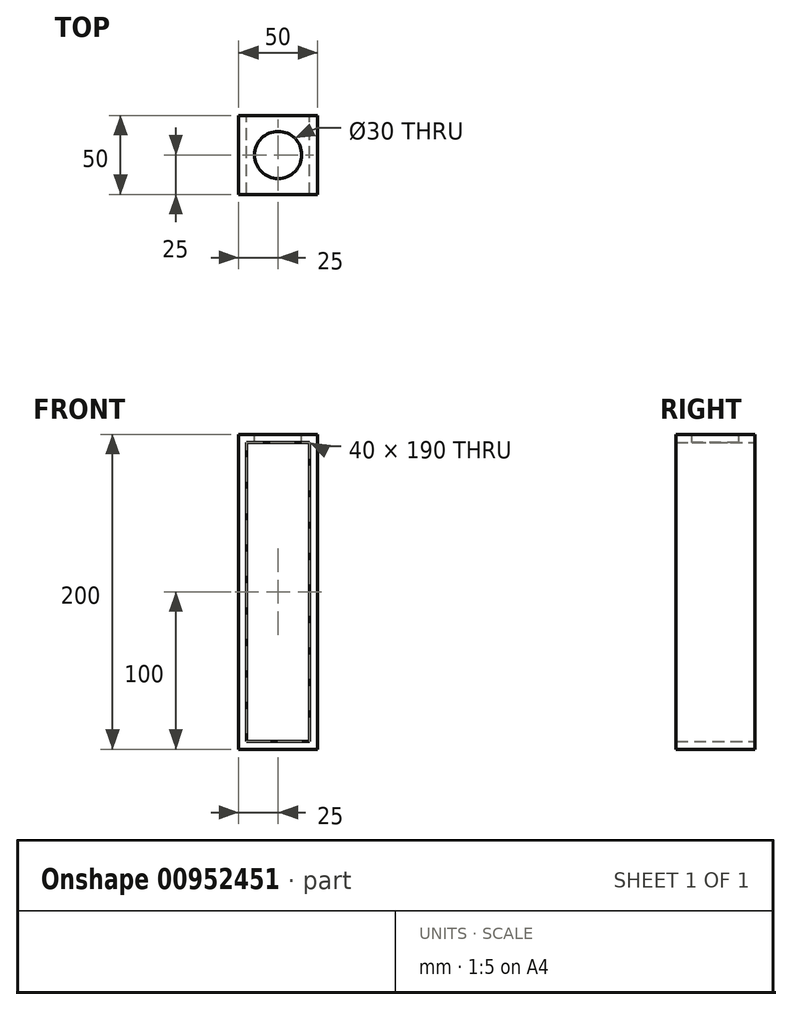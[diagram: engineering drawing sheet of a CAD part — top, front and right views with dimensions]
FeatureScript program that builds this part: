
annotation { "Feature Type Name" : "Feature", "Feature Type Description" : "" }
export const myFeature = defineFeature(function(context is Context, id is Id, definition is map)
    precondition{}
    {
        {
            var Q0;
            Q0=qCreatedBy(makeId("Front.planeOp"),FACE);
            var sketch = newSketch(context, id + "F0", { "sketchPlane" : qUnion([Q0])});
            skLineSegment(sketch, "E0.bottom", {"start": v(0, 0) * mm, "end": v(50, 0) * mm});
            skLineSegment(sketch, "E0.top", {"start": v(0, 200) * mm, "end": v(50, 200) * mm});
            skLineSegment(sketch, "E0.left", {"start": v(0, 0) * mm, "end": v(0, 200) * mm});
            skLineSegment(sketch, "E0.right", {"start": v(50, 0) * mm, "end": v(50, 200) * mm});
            skLineSegment(sketch, "E1.0", {"start": v(5, 5) * mm, "end": v(5, 195) * mm});
            skLineSegment(sketch, "E1.1", {"start": v(5, 5) * mm, "end": v(45, 5) * mm});
            skLineSegment(sketch, "E1.2", {"start": v(45, 5) * mm, "end": v(45, 195) * mm});
            skLineSegment(sketch, "E1.3", {"start": v(5, 195) * mm, "end": v(45, 195) * mm});
            skSolve(sketch);
        }
        {
            var Q0;
            Q0 = qSketchRegion(id + "F0", true);
            extrude(context, id + "F1", {"entities" : qUnion([Q0]), "depth" : 50 * mm, "offsetDistance" : 25 * mm});
        }
        {
            var Q0;
            Q0=makeQuery(id+"F1.opExtrude","SWEPT_FACE",FACE,{"disambiguationData":[OSD([sQuery(id+"F0.wireOp",EDGE,"E0.top")])]});
            var sketch = newSketch(context, id + "F2", { "sketchPlane" : qUnion([Q0])});
            skCircle(sketch, "E2", {"center": v(25, -25) * mm, "radius": 15 * mm});
            skPoint(sketch, "E2.centerSnap0", {"position": v(50, -25) * mm});
            skPoint(sketch, "E2.centerSnap1", {"position": v(25, 0) * mm});
            skSolve(sketch);
        }
        {
            var Q0;
            Q0 = qSketchRegion(id + "F2", true);
            extrude(context, id + "F3", {"entities" : qUnion([Q0]), "operationType" : NewBodyOperationType.REMOVE, "endBound" : BoundingType.UP_TO_NEXT, "oppositeDirection" : true, "depth" : 25 * mm, "offsetDistance" : 25 * mm});
        }
    });
